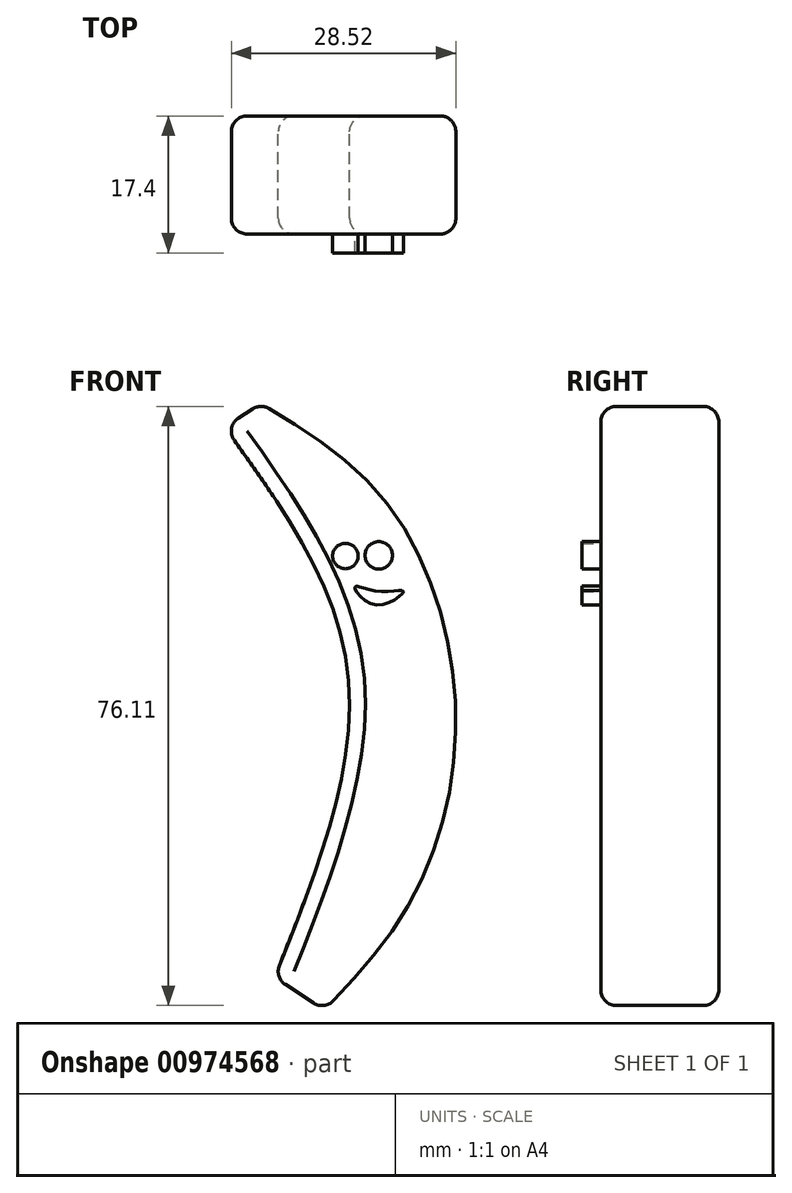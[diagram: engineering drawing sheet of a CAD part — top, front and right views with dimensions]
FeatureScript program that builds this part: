
annotation { "Feature Type Name" : "Feature", "Feature Type Description" : "" }
export const myFeature = defineFeature(function(context is Context, id is Id, definition is map)
    precondition{}
    {
        {
            var Q0;
            Q0=qCreatedBy(makeId("Front.planeOp"),FACE);
            var sketch = newSketch(context, id + "F0", { "sketchPlane" : qUnion([Q0])});
            skFitSpline(sketch, "E0", {"points": [v(-24.07, 48.54) * mm, v(-8.42, 17.43) * mm, v(-17.73, -21.4) * mm], "startDerivative": vector(44.58, -61.83) * mm, "endDerivative": vector(-31.04, -77.85) * mm});
            skLineSegment(sketch, "E1", {"start": v(-17.73, -21.4) * mm, "end": v(-11.4, -25.56) * mm});
            skLineSegment(sketch, "E2", {"start": v(-24.07, 48.54) * mm, "end": v(-19.51, 51.5) * mm});
            skFitSpline(sketch, "E3", {"points": [v(-19.51, 51.5) * mm, v(-3.27, 38.63) * mm, v(5.25, 13.27) * mm, v(0, -10.9) * mm, v(-11.4, -25.56) * mm], "startDerivative": vector(74.05, -44.26) * mm, "endDerivative": vector(-55.05, -58.5) * mm});
            skSolve(sketch);
        }
        {
            var Q0;
            Q0=makeQuery(id+"F0.imprint","IMPRINT",FACE,{"disambiguationData":[TD([[makeQuery(id+"F0.imprint","IMPRINT",EDGE,{"derivedFrom":sQuery(id+"F0.wireOp",EDGE,"E0")}),1.0]])]});
            extrude(context, id + "F1", {"entities" : qUnion([Q0]), "depth" : 15 * mm, "offsetDistance" : 25 * mm});
        }
        {
            var Q0;
            Q0=makeQuery(id+"F1.opExtrude","SWEPT_FACE",FACE,{"disambiguationData":[OSD([sQuery(id+"F0.wireOp",EDGE,"E0")])]});
            var Q1;
            Q1=makeQuery(id+"F1.opExtrude","SWEPT_FACE",FACE,{"disambiguationData":[OSD([sQuery(id+"F0.wireOp",EDGE,"E3")])]});
            var Q2;
            Q2=makeQuery(id+"F1.opExtrude","SWEPT_FACE",FACE,{"disambiguationData":[OSD([sQuery(id+"F0.wireOp",EDGE,"E2")])]});
            var Q3;
            Q3=makeQuery(id+"F1.opExtrude","SWEPT_FACE",FACE,{"disambiguationData":[OSD([sQuery(id+"F0.wireOp",EDGE,"E1")])]});
            fillet(context, id + "F2", {"entities" : qUnion([Q0, Q1, Q2, Q3]), "radius" : 2 * mm, "tangentPropagation" : true, "allowEdgeOverflow" : false});
        }
        {
            var Q0;
            Q0=makeQuery(id+"F1.opExtrude","CAP_FACE",FACE,{"disambiguationData":[OSD([sQuery(id+"F0.wireOp",EDGE,"E0"),sQuery(id+"F0.wireOp",EDGE,"E1"),sQuery(id+"F0.wireOp",EDGE,"E2"),sQuery(id+"F0.wireOp",EDGE,"E3")])],"isStart":false});
            var sketch = newSketch(context, id + "F3", { "sketchPlane" : qUnion([Q0])});
            skCircle(sketch, "E4", {"center": v(-8.74, 32.15) * mm, "radius": 1.62 * mm});
            skCircle(sketch, "E5", {"center": v(-4.5, 32.23) * mm, "radius": 1.74 * mm});
            skFitSpline(sketch, "E6", {"points": [v(-7.53, 28.23) * mm, v(-4.95, 25.95) * mm, v(-1.39, 27.64) * mm, v(-4.77, 27.68) * mm, v(-7.53, 28.23) * mm]});
            skSolve(sketch);
        }
        {
            var Q0;
            Q0=makeQuery(id+"F3.imprint","IMPRINT",FACE,{"disambiguationData":[TD([[makeQuery(id+"F3.imprint","IMPRINT",EDGE,{"derivedFrom":sQuery(id+"F3.wireOp",EDGE,"E4")}),1.0]])]});
            var Q1;
            Q1=makeQuery(id+"F3.imprint","IMPRINT",FACE,{"disambiguationData":[TD([[makeQuery(id+"F3.imprint","IMPRINT",EDGE,{"derivedFrom":sQuery(id+"F3.wireOp",EDGE,"E5")}),1.0]])]});
            var Q2;
            Q2=makeQuery(id+"F3.imprint","IMPRINT",FACE,{"disambiguationData":[TD([[makeQuery(id+"F3.imprint","IMPRINT",EDGE,{"derivedFrom":sQuery(id+"F3.wireOp",EDGE,"E6")}),1.0]])]});
            extrude(context, id + "F4", {"entities" : qUnion([Q0, Q1, Q2]), "operationType" : NewBodyOperationType.ADD, "depth" : 2.4 * mm, "offsetDistance" : 25 * mm});
        }
    });
